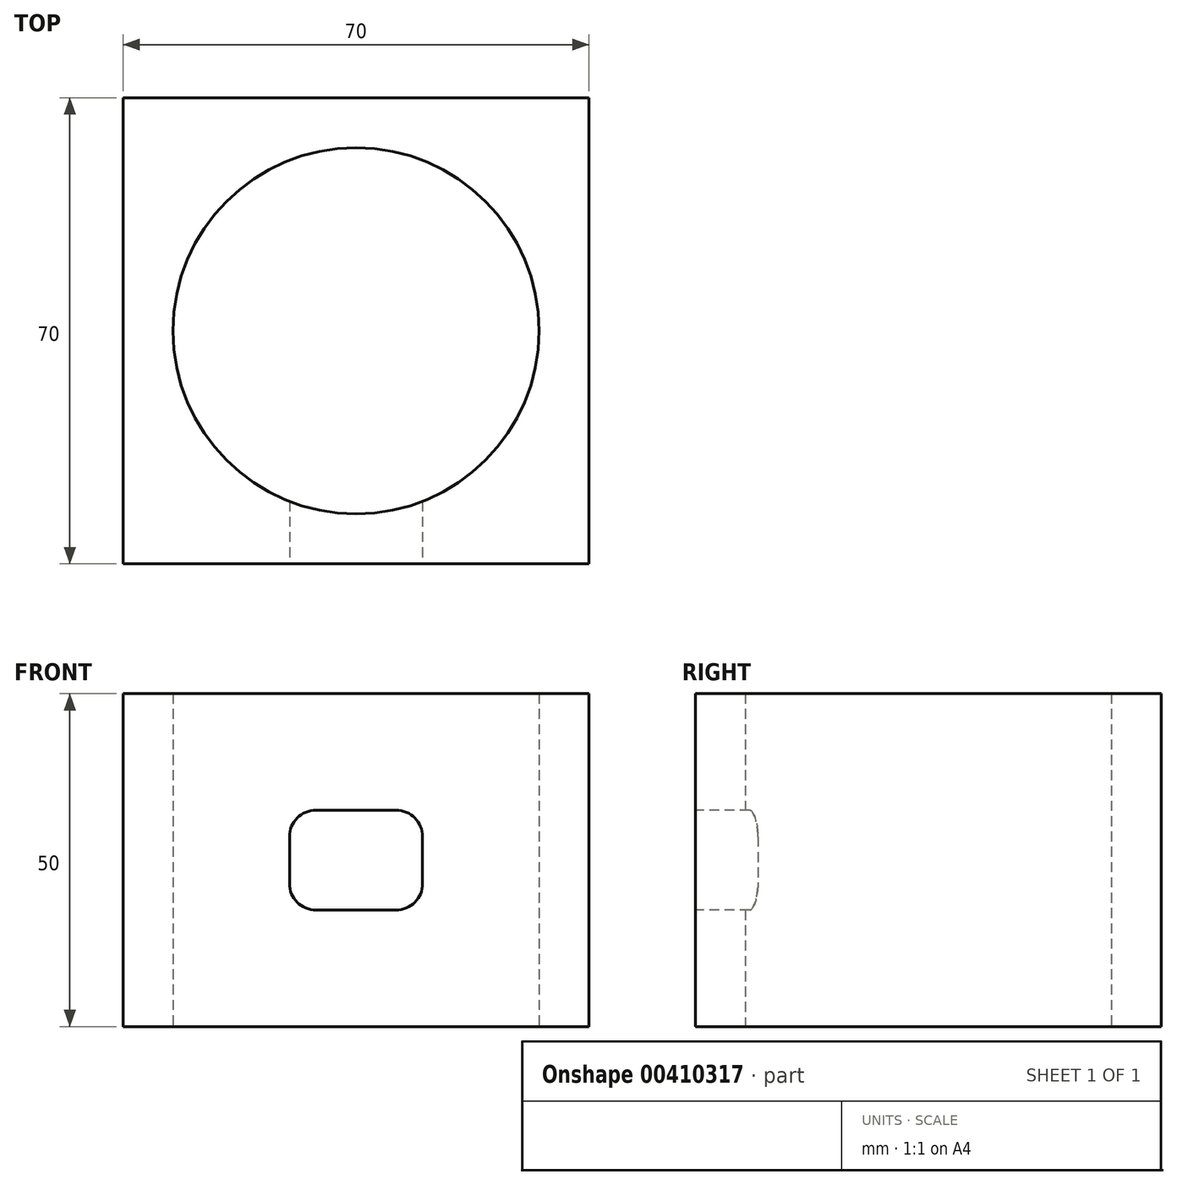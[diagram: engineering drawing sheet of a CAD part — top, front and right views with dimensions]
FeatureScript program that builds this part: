
annotation { "Feature Type Name" : "Feature", "Feature Type Description" : "" }
export const myFeature = defineFeature(function(context is Context, id is Id, definition is map)
    precondition{}
    {
        {
            var Q0;
            Q0=qCreatedBy(makeId("Top.planeOp"),FACE);
            var sketch = newSketch(context, id + "F0", { "sketchPlane" : qUnion([Q0])});
            skLineSegment(sketch, "E0.bottom", {"start": v(35, -35) * mm, "end": v(-35, -35) * mm});
            skLineSegment(sketch, "E0.top", {"start": v(35, 35) * mm, "end": v(-35, 35) * mm});
            skLineSegment(sketch, "E0.left", {"start": v(35, -35) * mm, "end": v(35, 35) * mm});
            skLineSegment(sketch, "E0.right", {"start": v(-35, -35) * mm, "end": v(-35, 35) * mm});
            skPoint(sketch, "E0.middle", {"position": v(0, 0) * mm});
            skCircle(sketch, "E1", {"center": v(0, 0) * mm, "radius": 27.5 * mm});
            skSolve(sketch);
        }
        {
            var Q0;
            Q0=makeQuery(id+"F0.imprint","IMPRINT",FACE,{"disambiguationData":[TD([[makeQuery(id+"F0.imprint","IMPRINT",EDGE,{"derivedFrom":sQuery(id+"F0.wireOp",EDGE,"E0.bottom")}),-1.0]])]});
            extrude(context, id + "F1", {"entities" : qUnion([Q0]), "depth" : 50 * mm});
        }
        {
            var Q0;
            Q0=makeQuery(id+"F1.opExtrude","SWEPT_FACE",FACE,{"disambiguationData":[OSD([sQuery(id+"F0.wireOp",EDGE,"E0.bottom")])]});
            var sketch = newSketch(context, id + "F2", { "sketchPlane" : qUnion([Q0])});
            skLineSegment(sketch, "E2.0.0", {"start": v(-35, 0) * mm, "end": v(35, 0) * mm});
            skLineSegment(sketch, "E2.0.1", {"start": v(35, 0) * mm, "end": v(35, 50) * mm});
            skLineSegment(sketch, "E2.0.2", {"start": v(35, 50) * mm, "end": v(-35, 50) * mm});
            skLineSegment(sketch, "E2.0.3", {"start": v(-35, 50) * mm, "end": v(-35, 0) * mm});
            skLineSegment(sketch, "E3.bottom", {"start": v(-10, 32.5) * mm, "end": v(10, 32.5) * mm});
            skLineSegment(sketch, "E3.top", {"start": v(-10, 17.5) * mm, "end": v(10, 17.5) * mm});
            skLineSegment(sketch, "E3.left", {"start": v(-10, 32.5) * mm, "end": v(-10, 17.5) * mm});
            skLineSegment(sketch, "E3.right", {"start": v(10, 32.5) * mm, "end": v(10, 17.5) * mm});
            skSolve(sketch);
        }
        {
            var Q0;
            Q0=makeQuery(id+"F2.imprint","IMPRINT",FACE,{"disambiguationData":[TD([[makeQuery(id+"F2.imprint","IMPRINT",EDGE,{"derivedFrom":sQuery(id+"F2.wireOp",EDGE,"E3.bottom")}),-1.0]])]});
            extrude(context, id + "F3", {"entities" : qUnion([Q0]), "operationType" : NewBodyOperationType.REMOVE, "oppositeDirection" : true, "depth" : 25 * mm});
        }
        {
            var Q0;
            Q0=makeQuery(id+"F3.boolean.opBoolean","COPY",EDGE,{"derivedFrom":makeQuery(id+"F3.opExtrude","SWEPT_EDGE",EDGE,{"disambiguationData":[OSD([sQuery(id+"F2.wireOp",EDGE,"E3.bottom"),sQuery(id+"F2.wireOp",EDGE,"E3.left")])]})});
            var Q1;
            Q1=makeQuery(id+"F3.boolean.opBoolean","COPY",EDGE,{"derivedFrom":makeQuery(id+"F3.opExtrude","SWEPT_EDGE",EDGE,{"disambiguationData":[OSD([sQuery(id+"F2.wireOp",EDGE,"E3.bottom"),sQuery(id+"F2.wireOp",EDGE,"E3.right")])]})});
            var Q2;
            Q2=makeQuery(id+"F3.boolean.opBoolean","COPY",EDGE,{"derivedFrom":makeQuery(id+"F3.opExtrude","SWEPT_EDGE",EDGE,{"disambiguationData":[OSD([sQuery(id+"F2.wireOp",EDGE,"E3.top"),sQuery(id+"F2.wireOp",EDGE,"E3.right")])]})});
            var Q3;
            Q3=makeQuery(id+"F3.boolean.opBoolean","COPY",EDGE,{"derivedFrom":makeQuery(id+"F3.opExtrude","SWEPT_EDGE",EDGE,{"disambiguationData":[OSD([sQuery(id+"F2.wireOp",EDGE,"E3.top"),sQuery(id+"F2.wireOp",EDGE,"E3.left")])]})});
            fillet(context, id + "F4", {"entities" : qUnion([Q0, Q1, Q2, Q3]), "radius" : 4 * mm, "tangentPropagation" : true, "allowEdgeOverflow" : false});
        }
    });
